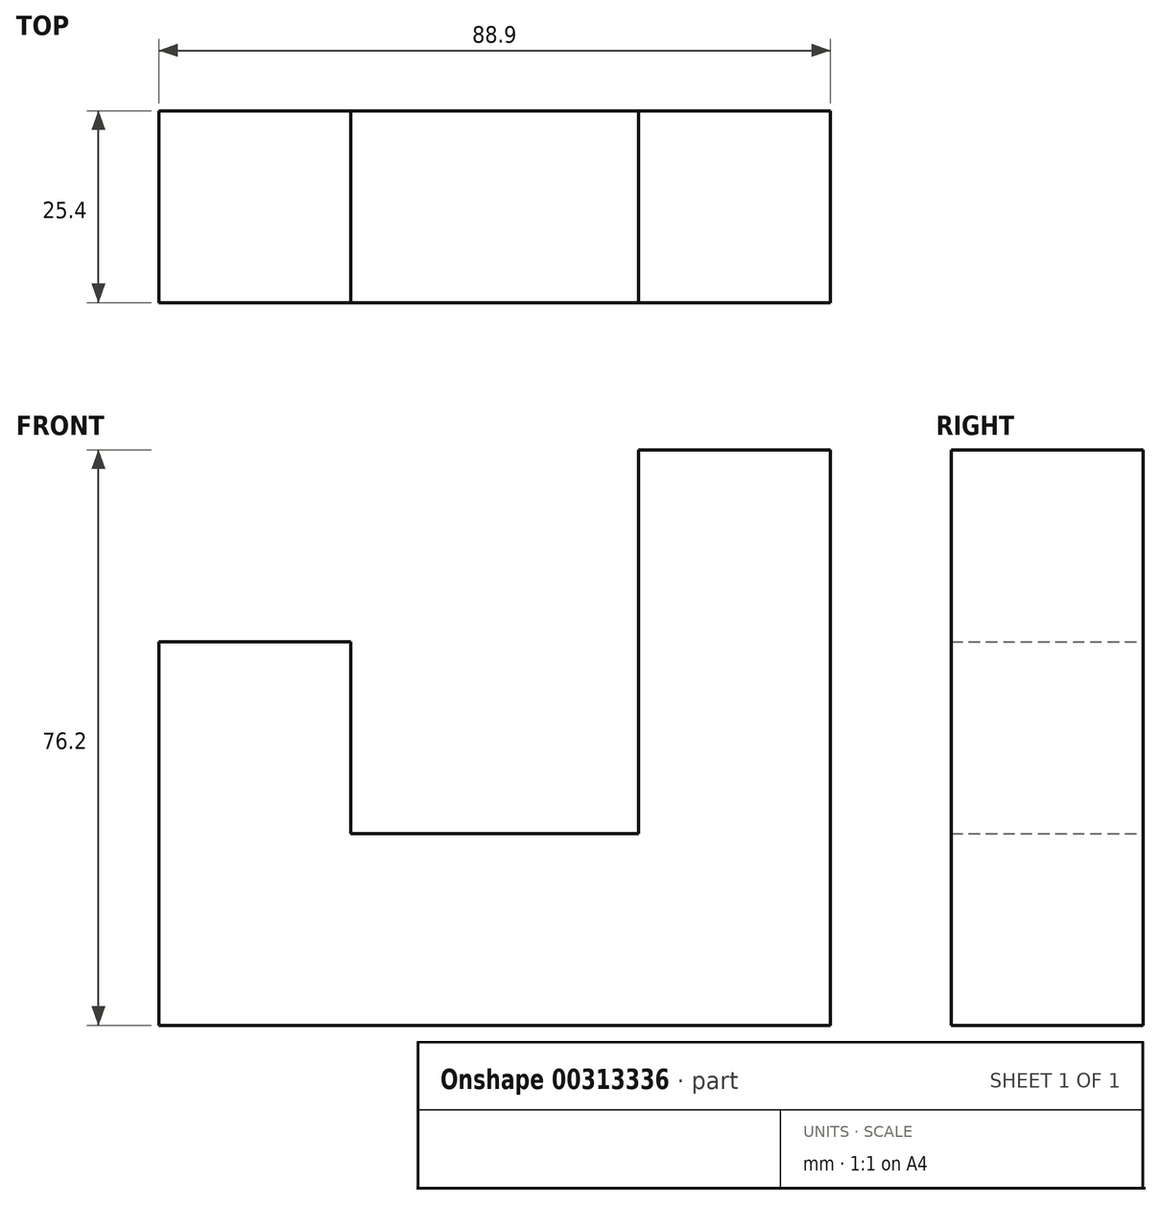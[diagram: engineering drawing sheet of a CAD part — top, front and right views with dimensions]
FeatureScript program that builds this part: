
annotation { "Feature Type Name" : "Feature", "Feature Type Description" : "" }
export const myFeature = defineFeature(function(context is Context, id is Id, definition is map)
    precondition{}
    {
        {
            var Q0;
            Q0=qCreatedBy(makeId("Front.planeOp"),FACE);
            var sketch = newSketch(context, id + "F0", { "sketchPlane" : qUnion([Q0])});
            skLineSegment(sketch, "E0", {"start": v(-31.6, -36.37) * mm, "end": v(57.3, -36.37) * mm});
            skLineSegment(sketch, "E1", {"start": v(-31.6, -36.37) * mm, "end": v(-31.6, 14.43) * mm});
            skLineSegment(sketch, "E2", {"start": v(-31.6, 14.43) * mm, "end": v(-6.2, 14.43) * mm});
            skLineSegment(sketch, "E3", {"start": v(-6.2, 14.43) * mm, "end": v(-6.2, -10.97) * mm});
            skLineSegment(sketch, "E4", {"start": v(-6.2, -10.97) * mm, "end": v(31.9, -10.97) * mm});
            skLineSegment(sketch, "E5", {"start": v(31.9, -10.97) * mm, "end": v(31.9, 39.83) * mm});
            skLineSegment(sketch, "E6", {"start": v(31.9, 39.83) * mm, "end": v(57.3, 39.83) * mm});
            skLineSegment(sketch, "E7", {"start": v(57.3, 39.83) * mm, "end": v(57.3, -36.37) * mm});
            skSolve(sketch);
        }
        {
            var Q0;
            Q0=makeQuery(id+"F0.imprint","IMPRINT",FACE,{"disambiguationData":[TD([[makeQuery(id+"F0.imprint","IMPRINT",EDGE,{"derivedFrom":sQuery(id+"F0.wireOp",EDGE,"E0")}),1.0]])]});
            extrude(context, id + "F1", {"entities" : qUnion([Q0]), "depth" : 25.4 * mm});
        }
    });
